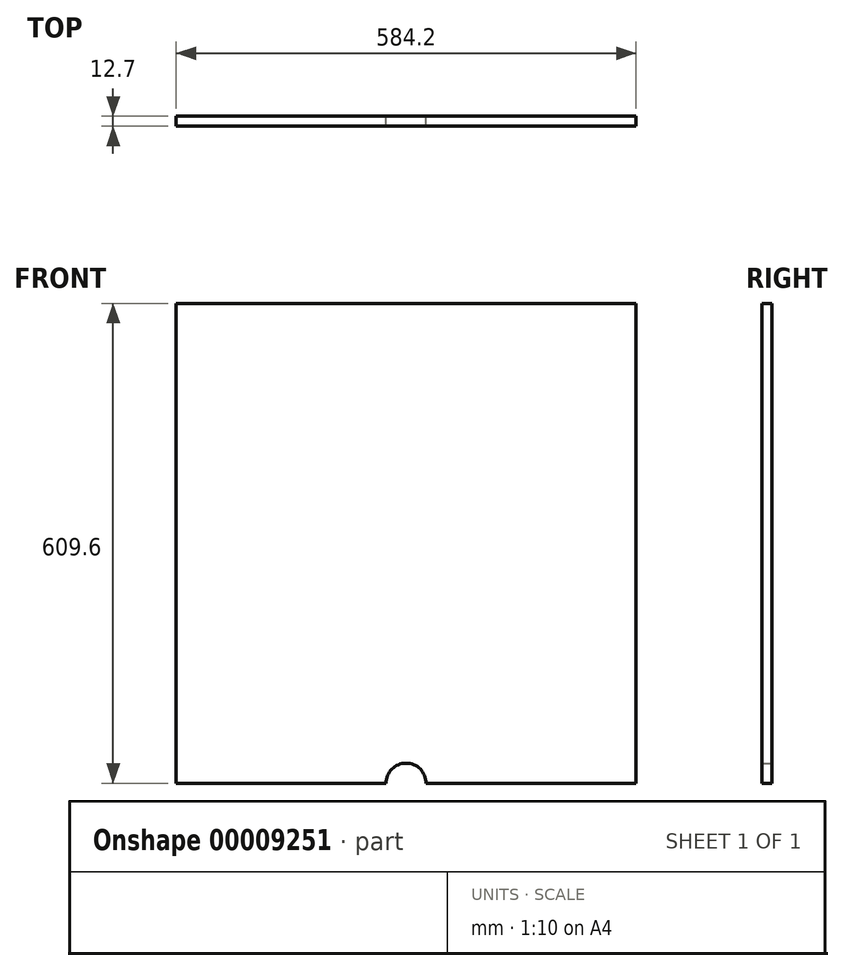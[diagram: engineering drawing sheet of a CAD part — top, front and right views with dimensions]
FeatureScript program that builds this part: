
annotation { "Feature Type Name" : "Feature", "Feature Type Description" : "" }
export const myFeature = defineFeature(function(context is Context, id is Id, definition is map)
    precondition{}
    {
        {
            var Q0;
            Q0=qCreatedBy(makeId("Front.planeOp"),FACE);
            var sketch = newSketch(context, id + "F0", { "sketchPlane" : qUnion([Q0])});
            skLineSegment(sketch, "E0.rect.bottom", {"start": v(292.1, 304.8) * mm, "end": v(-292.1, 304.8) * mm});
            skLineSegment(sketch, "E0.rect.top", {"start": v(292.1, -304.8) * mm, "end": v(25.4, -304.8) * mm});
            skLineSegment(sketch, "E0.rect.left", {"start": v(292.1, 304.8) * mm, "end": v(292.1, -304.8) * mm});
            skLineSegment(sketch, "E0.rect.right", {"start": v(-292.1, 304.8) * mm, "end": v(-292.1, -304.8) * mm});
            skPoint(sketch, "E0.rect.middle", {"position": v(0, 0) * mm});
            skArc(sketch, "E1", {"start": v(25.4, -304.8) * mm, "mid": v(0, -279.4) * mm, "end": v(-25.4, -304.8) * mm});
            skLineSegment(sketch, "E2.trimOffspring", {"start": v(-25.4, -304.8) * mm, "end": v(-292.1, -304.8) * mm});
            skSolve(sketch);
        }
        {
            var Q0;
            Q0=makeQuery(id+"F0.imprint","IMPRINT",FACE,{"disambiguationData":[TD([[makeQuery(id+"F0.imprint","IMPRINT",EDGE,{"derivedFrom":sQuery(id+"F0.wireOp",EDGE,"E0.rect.bottom")}),1.0]])]});
            extrude(context, id + "F1", {"entities" : qUnion([Q0]), "depth" : 12.7 * mm});
        }
    });
